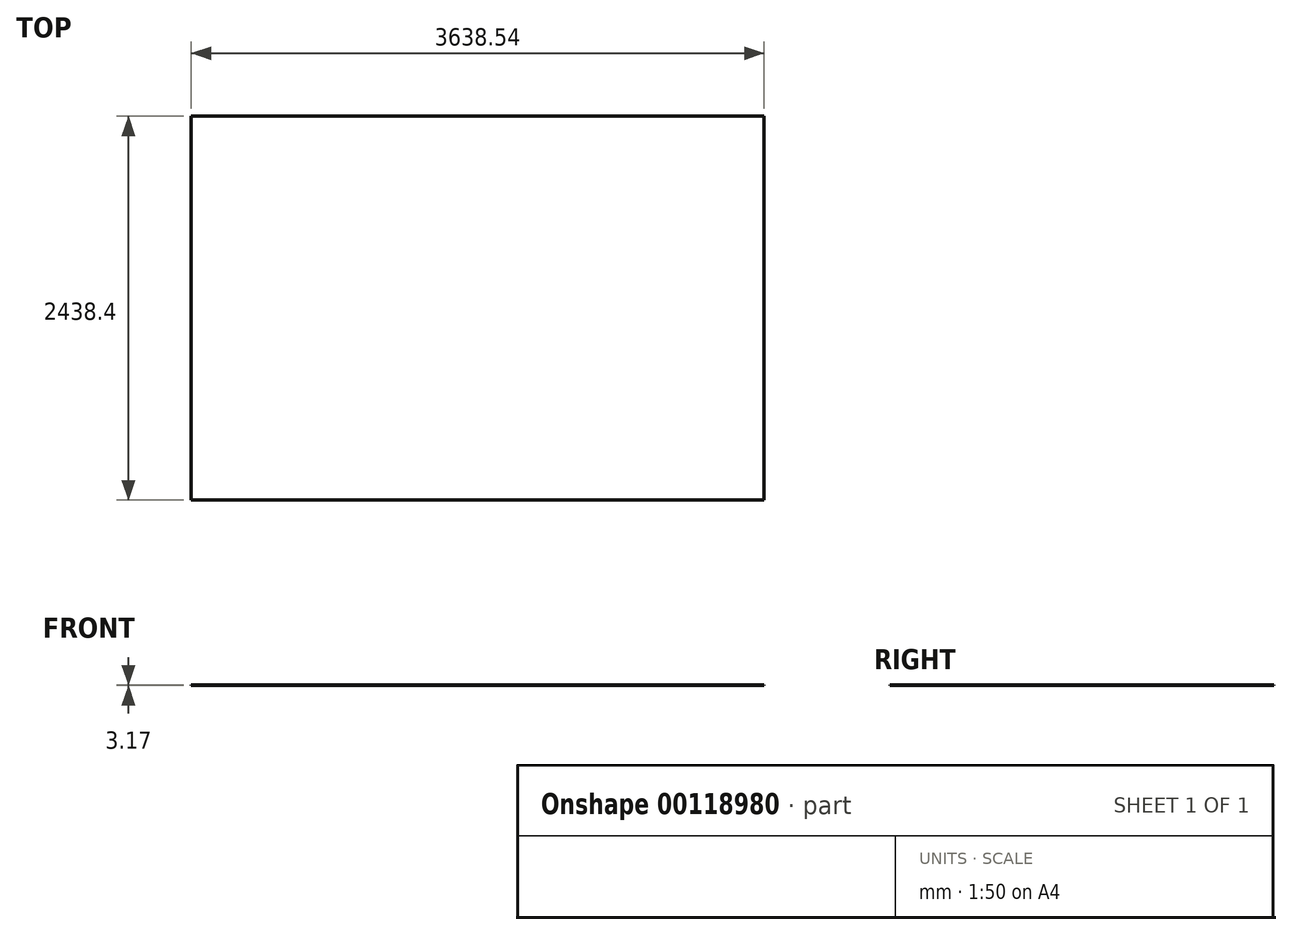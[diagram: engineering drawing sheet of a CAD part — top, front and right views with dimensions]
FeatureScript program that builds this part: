
annotation { "Feature Type Name" : "Feature", "Feature Type Description" : "" }
export const myFeature = defineFeature(function(context is Context, id is Id, definition is map)
    precondition{}
    {
        {
            var Q0;
            Q0=qCreatedBy(makeId("Top.planeOp"),FACE);
            var sketch = newSketch(context, id + "F0", { "sketchPlane" : qUnion([Q0])});
            skLineSegment(sketch, "E0.bottom", {"start": v(1819.27, 1219.2) * mm, "end": v(-1819.28, 1219.2) * mm});
            skLineSegment(sketch, "E0.top", {"start": v(1819.28, -1219.2) * mm, "end": v(-1819.28, -1219.2) * mm});
            skLineSegment(sketch, "E0.left", {"start": v(1819.28, 1219.2) * mm, "end": v(1819.28, -1219.2) * mm});
            skLineSegment(sketch, "E0.right", {"start": v(-1819.27, 1219.2) * mm, "end": v(-1819.28, -1219.2) * mm});
            skPoint(sketch, "E0.middle", {"position": v(0, 0) * mm});
            skSolve(sketch);
        }
        {
            var Q0;
            Q0 = qSketchRegion(id + "F0", true);
            extrude(context, id + "F1", {"entities" : qUnion([Q0]), "depth" : 3.17 * mm});
        }
    });
